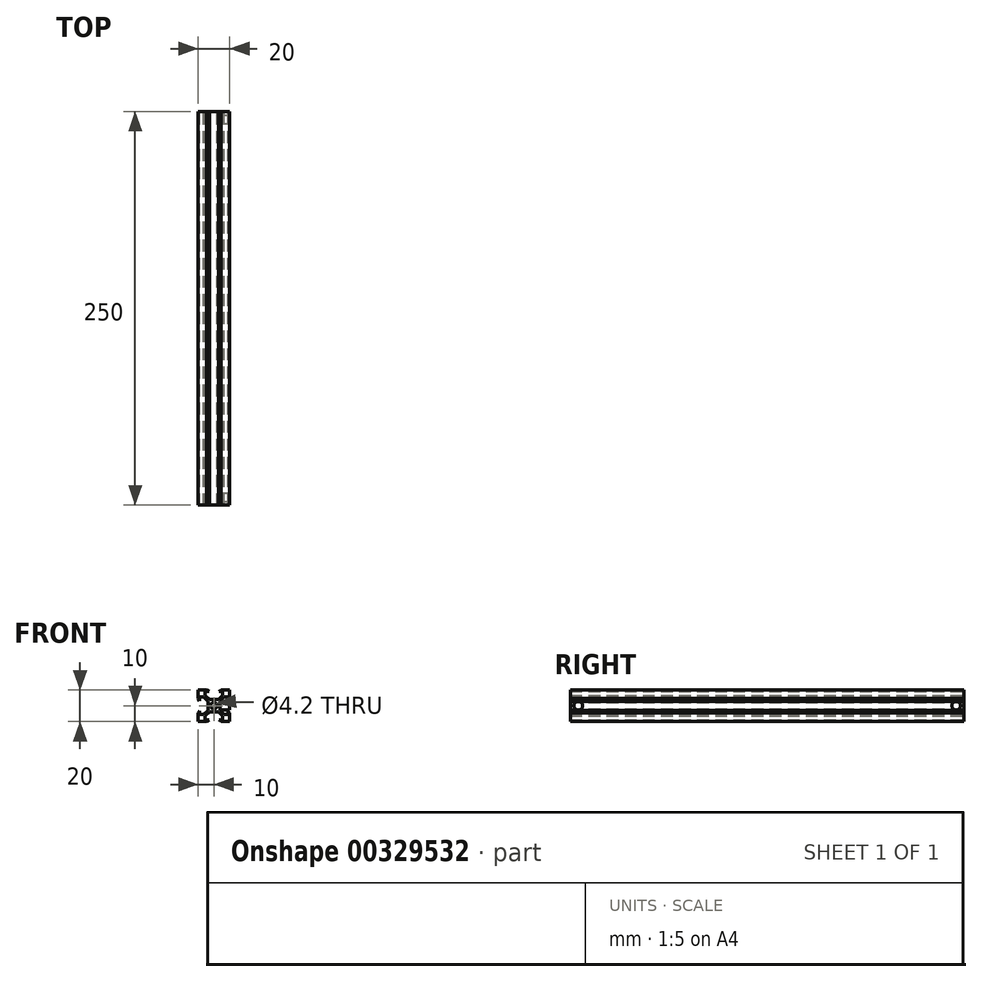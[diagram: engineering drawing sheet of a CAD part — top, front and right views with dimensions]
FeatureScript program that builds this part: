
annotation { "Feature Type Name" : "Feature", "Feature Type Description" : "" }
export const myFeature = defineFeature(function(context is Context, id is Id, definition is map)
    precondition{}
    {
        {
            var Q0;
            Q0=qCreatedBy(makeId("Front.planeOp"),FACE);
            var sketch = newSketch(context, id + "F0", { "sketchPlane" : qUnion([Q0])});
            skCircle(sketch, "E0", {"center": v(0, 0) * mm, "radius": 2.1 * mm});
            skLineSegment(sketch, "E1.bottom", {"start": v(3.9, 3.9) * mm, "end": v(-3.9, 3.9) * mm});
            skLineSegment(sketch, "E1.top", {"start": v(3.9, -3.9) * mm, "end": v(-3.9, -3.9) * mm});
            skLineSegment(sketch, "E1.left", {"start": v(3.9, 3.9) * mm, "end": v(3.9, -3.9) * mm});
            skLineSegment(sketch, "E1.right", {"start": v(-3.9, 3.9) * mm, "end": v(-3.9, -3.9) * mm});
            skLineSegment(sketch, "E2.bottom", {"start": v(10, 10) * mm, "end": v(-10, 10) * mm, "construction": true});
            skLineSegment(sketch, "E2.top", {"start": v(10, -10) * mm, "end": v(-10, -10) * mm, "construction": true});
            skLineSegment(sketch, "E2.left", {"start": v(10, 10) * mm, "end": v(10, -10) * mm, "construction": true});
            skLineSegment(sketch, "E2.right", {"start": v(-10, 10) * mm, "end": v(-10, -10) * mm, "construction": true});
            skLineSegment(sketch, "E3", {"start": v(-10, 10) * mm, "end": v(-3.9, 3.9) * mm, "construction": true});
            skLineSegment(sketch, "E4", {"start": v(-10, 10) * mm, "end": v(-10, 4.58) * mm});
            skLineSegment(sketch, "E5", {"start": v(-10, 4.58) * mm, "end": v(-9.1, 3.12) * mm});
            skLineSegment(sketch, "E6", {"start": v(-9.1, 3.12) * mm, "end": v(-9.1, 5.5) * mm});
            skLineSegment(sketch, "E7", {"start": v(-9.1, 5.5) * mm, "end": v(-6.56, 5.5) * mm});
            skLineSegment(sketch, "E8", {"start": v(-6.56, 5.5) * mm, "end": v(-3.9, 2.84) * mm});
            skLineSegment(sketch, "E9", {"start": v(-2.84, 3.9) * mm, "end": v(-5.5, 6.56) * mm});
            skLineSegment(sketch, "E10", {"start": v(-5.5, 6.56) * mm, "end": v(-5.5, 9.1) * mm});
            skLineSegment(sketch, "E11", {"start": v(-5.5, 9.1) * mm, "end": v(-3.13, 9.1) * mm});
            skLineSegment(sketch, "E12", {"start": v(-3.13, 9.1) * mm, "end": v(-4.58, 10) * mm});
            skLineSegment(sketch, "E13", {"start": v(-4.58, 10) * mm, "end": v(-10, 10) * mm});
            skLineSegment(sketch, "E14.1.0", {"start": v(-5.5, -6.56) * mm, "end": v(-2.84, -3.9) * mm});
            skLineSegment(sketch, "E14.1.1", {"start": v(-5.5, -9.1) * mm, "end": v(-5.5, -6.56) * mm});
            skLineSegment(sketch, "E14.1.2", {"start": v(-3.13, -9.1) * mm, "end": v(-5.5, -9.1) * mm});
            skLineSegment(sketch, "E14.1.3", {"start": v(-4.58, -10) * mm, "end": v(-3.13, -9.1) * mm});
            skLineSegment(sketch, "E14.1.4", {"start": v(-6.56, -5.5) * mm, "end": v(-9.1, -5.5) * mm});
            skLineSegment(sketch, "E14.1.5", {"start": v(-3.9, -2.84) * mm, "end": v(-6.56, -5.5) * mm});
            skLineSegment(sketch, "E14.1.6", {"start": v(-9.1, -5.5) * mm, "end": v(-9.1, -3.13) * mm});
            skLineSegment(sketch, "E14.1.7", {"start": v(-9.1, -3.13) * mm, "end": v(-10, -4.58) * mm});
            skLineSegment(sketch, "E14.2.0", {"start": v(6.56, -5.5) * mm, "end": v(3.9, -2.84) * mm});
            skLineSegment(sketch, "E14.2.1", {"start": v(9.1, -5.5) * mm, "end": v(6.56, -5.5) * mm});
            skLineSegment(sketch, "E14.2.2", {"start": v(9.1, -3.13) * mm, "end": v(9.1, -5.5) * mm});
            skLineSegment(sketch, "E14.2.3", {"start": v(10, -4.58) * mm, "end": v(9.1, -3.12) * mm});
            skLineSegment(sketch, "E14.2.4", {"start": v(5.5, -6.56) * mm, "end": v(5.5, -9.1) * mm});
            skLineSegment(sketch, "E14.2.5", {"start": v(2.84, -3.9) * mm, "end": v(5.5, -6.56) * mm});
            skLineSegment(sketch, "E14.2.6", {"start": v(5.5, -9.1) * mm, "end": v(3.13, -9.1) * mm});
            skLineSegment(sketch, "E14.2.7", {"start": v(3.13, -9.1) * mm, "end": v(4.58, -10) * mm});
            skLineSegment(sketch, "E14.3.0", {"start": v(5.5, 6.56) * mm, "end": v(2.84, 3.9) * mm});
            skLineSegment(sketch, "E14.3.1", {"start": v(5.5, 9.1) * mm, "end": v(5.5, 6.56) * mm});
            skLineSegment(sketch, "E14.3.2", {"start": v(3.13, 9.1) * mm, "end": v(5.5, 9.1) * mm});
            skLineSegment(sketch, "E14.3.3", {"start": v(4.58, 10) * mm, "end": v(3.12, 9.1) * mm});
            skLineSegment(sketch, "E14.3.4", {"start": v(6.56, 5.5) * mm, "end": v(9.1, 5.5) * mm});
            skLineSegment(sketch, "E14.3.5", {"start": v(3.9, 2.84) * mm, "end": v(6.56, 5.5) * mm});
            skLineSegment(sketch, "E14.3.6", {"start": v(9.1, 5.5) * mm, "end": v(9.1, 3.13) * mm});
            skLineSegment(sketch, "E14.3.7", {"start": v(9.1, 3.13) * mm, "end": v(10, 4.58) * mm});
            skLineSegment(sketch, "E15", {"start": v(4.58, 10) * mm, "end": v(10, 10) * mm});
            skLineSegment(sketch, "E16", {"start": v(10, 4.58) * mm, "end": v(10, 10) * mm});
            skLineSegment(sketch, "E17", {"start": v(10, -4.58) * mm, "end": v(10, -10) * mm});
            skLineSegment(sketch, "E18", {"start": v(4.58, -10) * mm, "end": v(10, -10) * mm});
            skLineSegment(sketch, "E19", {"start": v(-4.58, -10) * mm, "end": v(-10, -10) * mm});
            skLineSegment(sketch, "E20", {"start": v(-10, -4.58) * mm, "end": v(-10, -10) * mm});
            skSolve(sketch);
        }
        {
            var Q0;
            Q0 = qSketchRegion(id + "F0", true);
            extrude(context, id + "F1", {"entities" : qUnion([Q0]), "endBound" : BoundingType.SYMMETRIC, "depth" : 250 * mm});
        }
        {
            var Q0;
            Q0=makeQuery(id+"F1.opExtrude","SWEPT_FACE",FACE,{"disambiguationData":[OSD([sQuery(id+"F0.wireOp",EDGE,"E16")])]});
            var sketch = newSketch(context, id + "F2", { "sketchPlane" : qUnion([Q0])});
            skPoint(sketch, "E21", {"position": v(-120, 0) * mm});
            skPoint(sketch, "E22", {"position": v(120, 0) * mm});
            skCircle(sketch, "E23", {"center": v(-120, 0) * mm, "radius": 2.75 * mm});
            skCircle(sketch, "E24", {"center": v(120, 0) * mm, "radius": 2.75 * mm});
            skSolve(sketch);
        }
        {
            var Q0;
            Q0 = qSketchRegion(id + "F2", true);
            extrude(context, id + "F3", {"entities" : qUnion([Q0]), "operationType" : NewBodyOperationType.ADD, "endBound" : BoundingType.UP_TO_NEXT, "oppositeDirection" : true, "depth" : 25 * mm});
        }
    });
